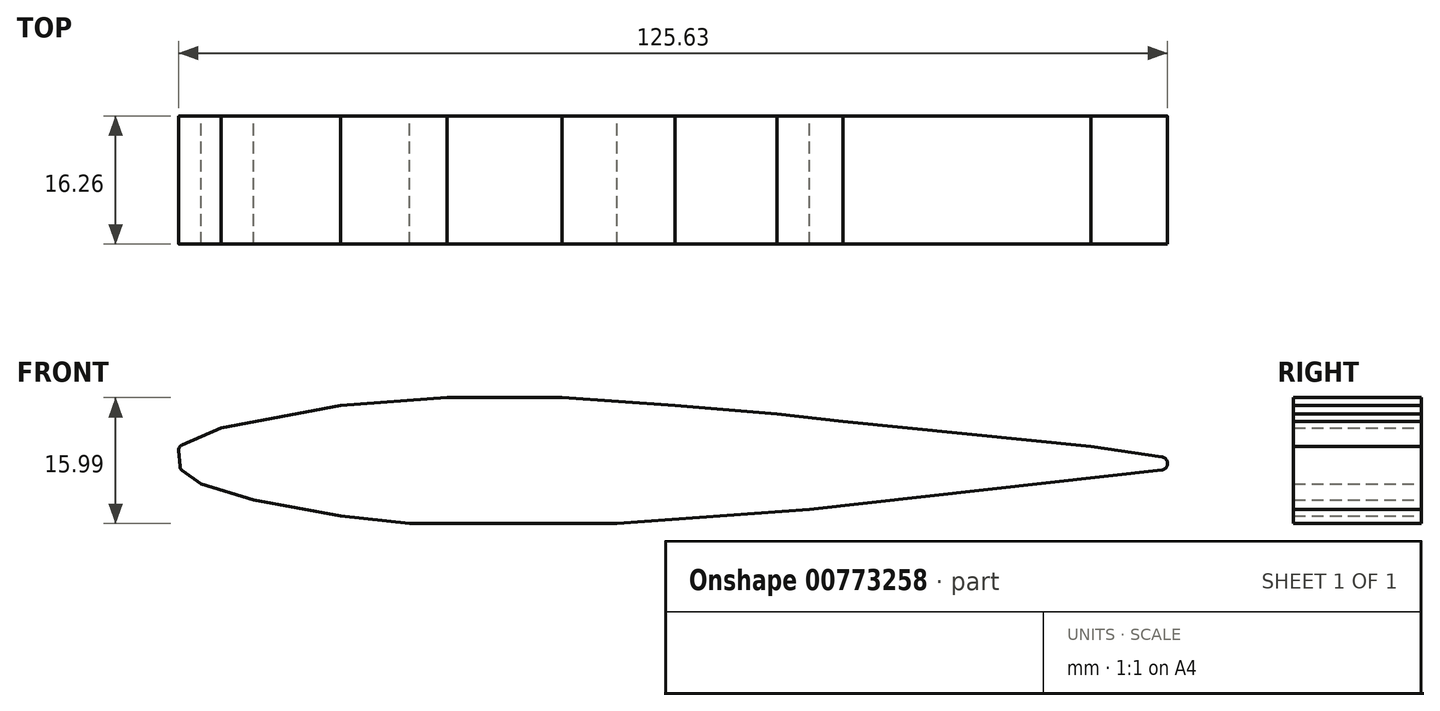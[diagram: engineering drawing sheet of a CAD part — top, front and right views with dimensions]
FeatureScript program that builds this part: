
annotation { "Feature Type Name" : "Feature", "Feature Type Description" : "" }
export const myFeature = defineFeature(function(context is Context, id is Id, definition is map)
    precondition{}
    {
        {
            var Q0;
            Q0=qCreatedBy(makeId("Front.planeOp"),FACE);
            var sketch = newSketch(context, id + "F0", { "sketchPlane" : qUnion([Q0])});
            skLineSegment(sketch, "E0", {"start": v(72.88, 0.97) * mm, "end": v(28.14, -4.02) * mm});
            skLineSegment(sketch, "E1", {"start": v(28.14, -4.02) * mm, "end": v(3.68, -5.82) * mm});
            skLineSegment(sketch, "E2", {"start": v(3.68, -5.82) * mm, "end": v(-22.69, -5.82) * mm});
            skLineSegment(sketch, "E3", {"start": v(-22.69, -5.82) * mm, "end": v(-31.4, -4.87) * mm});
            skLineSegment(sketch, "E4", {"start": v(-31.4, -4.87) * mm, "end": v(-42.47, -2.85) * mm});
            skLineSegment(sketch, "E5", {"start": v(-42.47, -2.85) * mm, "end": v(-49.17, -0.82) * mm});
            skLineSegment(sketch, "E6", {"start": v(-49.17, -0.82) * mm, "end": v(-51.56, 0.9) * mm});
            skLineSegment(sketch, "E7", {"start": v(-51.85, 1.42) * mm, "end": v(-52, 3.46) * mm});
            skLineSegment(sketch, "E8", {"start": v(-51.58, 4.16) * mm, "end": v(-46.62, 6.3) * mm});
            skLineSegment(sketch, "E9", {"start": v(-46.62, 6.3) * mm, "end": v(-31.4, 9.17) * mm});
            skLineSegment(sketch, "E10", {"start": v(-31.4, 9.17) * mm, "end": v(-17.93, 10.17) * mm});
            skLineSegment(sketch, "E11", {"start": v(-17.93, 10.17) * mm, "end": v(-3.33, 10.17) * mm});
            skLineSegment(sketch, "E12", {"start": v(-3.33, 10.17) * mm, "end": v(11.02, 9.17) * mm});
            skLineSegment(sketch, "E13", {"start": v(11.02, 9.17) * mm, "end": v(24, 8.1) * mm});
            skLineSegment(sketch, "E14", {"start": v(24, 8.1) * mm, "end": v(32.4, 7.15) * mm});
            skLineSegment(sketch, "E15", {"start": v(32.4, 7.15) * mm, "end": v(63.88, 3.96) * mm});
            skLineSegment(sketch, "E16", {"start": v(63.88, 3.96) * mm, "end": v(72.9, 2.62) * mm});
            skPoint(sketch, "E17.visualSharp", {"position": v(-52.04, 3.96) * mm});
            skArc(sketch, "E17.filletArc", {"start": v(-51.58, 4.16) * mm, "mid": v(-51.9, 3.88) * mm, "end": v(-52, 3.46) * mm});
            skPoint(sketch, "E18.visualSharp", {"position": v(-51.83, 1.09) * mm});
            skArc(sketch, "E18.filletArc", {"start": v(-51.85, 1.42) * mm, "mid": v(-51.76, 1.12) * mm, "end": v(-51.56, 0.9) * mm});
            skArc(sketch, "E19.filletArc", {"start": v(72.88, 0.97) * mm, "mid": v(73.62, 1.78) * mm, "end": v(72.9, 2.62) * mm});
            skSolve(sketch);
        }
        {
            var Q0;
            Q0=makeQuery(id+"F0.imprint","IMPRINT",FACE,{"disambiguationData":[TD([[makeQuery(id+"F0.imprint","IMPRINT",EDGE,{"derivedFrom":sQuery(id+"F0.wireOp",EDGE,"E0")}),-1.0]])]});
            extrude(context, id + "F1", {"entities" : qUnion([Q0]), "depth" : 16.26 * mm, "offsetDistance" : 25.4 * mm});
        }
    });
